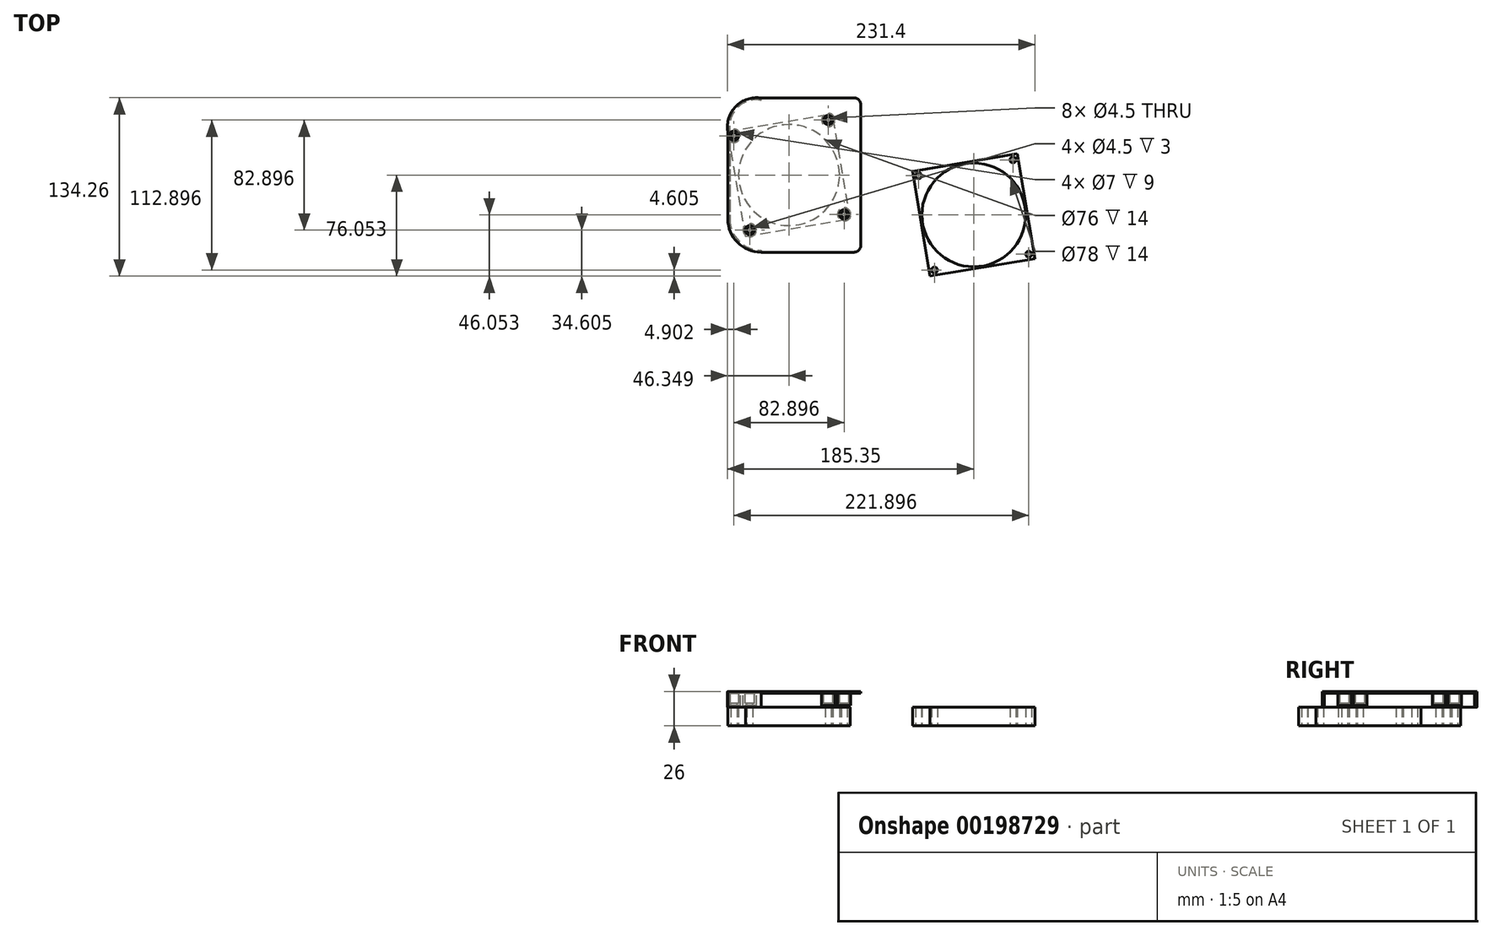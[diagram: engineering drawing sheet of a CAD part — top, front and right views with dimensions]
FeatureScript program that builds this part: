
annotation { "Feature Type Name" : "Feature", "Feature Type Description" : "" }
export const myFeature = defineFeature(function(context is Context, id is Id, definition is map)
    precondition{}
    {
        {
            var Q0;
            Q0=qCreatedBy(makeId("Top.planeOp"),FACE);
            var sketch = newSketch(context, id + "F0", { "sketchPlane" : qUnion([Q0])});
            skLineSegment(sketch, "E0.bottom", {"start": v(0, 0) * mm, "end": v(80, 0) * mm});
            skLineSegment(sketch, "E0.top", {"start": v(0, 80) * mm, "end": v(80, 80) * mm});
            skLineSegment(sketch, "E0.left", {"start": v(0, 0) * mm, "end": v(0, 80) * mm});
            skLineSegment(sketch, "E0.right", {"start": v(80, 0) * mm, "end": v(80, 80) * mm});
            skLineSegment(sketch, "E1.bottom", {"start": v(139, 50) * mm, "end": v(219, 50) * mm});
            skLineSegment(sketch, "E1.top", {"start": v(139, -30) * mm, "end": v(219, -30) * mm});
            skLineSegment(sketch, "E1.left", {"start": v(139, 50) * mm, "end": v(139, -30) * mm});
            skLineSegment(sketch, "E1.right", {"start": v(219, 50) * mm, "end": v(219, -30) * mm});
            skCircle(sketch, "E2", {"center": v(40, 40) * mm, "radius": 38 * mm});
            skCircle(sketch, "E3", {"center": v(179, 10) * mm, "radius": 39 * mm});
            skCircle(sketch, "E4", {"center": v(4, 76) * mm, "radius": 2.25 * mm});
            skCircle(sketch, "E5", {"center": v(76, 76) * mm, "radius": 2.25 * mm});
            skCircle(sketch, "E6", {"center": v(76, 4) * mm, "radius": 2.25 * mm});
            skCircle(sketch, "E7", {"center": v(4, 4) * mm, "radius": 2.25 * mm});
            skCircle(sketch, "E8", {"center": v(143, 46) * mm, "radius": 2.25 * mm});
            skCircle(sketch, "E9", {"center": v(215, 46) * mm, "radius": 2.25 * mm});
            skCircle(sketch, "E10", {"center": v(215, -26) * mm, "radius": 2.25 * mm});
            skCircle(sketch, "E11", {"center": v(143, -26) * mm, "radius": 2.25 * mm});
            skSolve(sketch);
        }
        {
            var Q0;
            Q0=qSketchRegion(id+"F0",true);
            extrude(context, id + "F1", {"entities" : qUnion([Q0]), "depth" : 14 * mm});
        }
        {
            var Q0;
            Q0=makeQuery(id+"F1.opExtrude","SWEPT_BODY",BODY,{"disambiguationData":[OSD([sQuery(id+"F0.wireOp",EDGE,"E0.bottom"),sQuery(id+"F0.wireOp",EDGE,"E0.top"),sQuery(id+"F0.wireOp",EDGE,"E0.left"),sQuery(id+"F0.wireOp",EDGE,"E0.right"),sQuery(id+"F0.wireOp",EDGE,"E2"),sQuery(id+"F0.wireOp",EDGE,"E4"),sQuery(id+"F0.wireOp",EDGE,"E5"),sQuery(id+"F0.wireOp",EDGE,"E6"),sQuery(id+"F0.wireOp",EDGE,"E7")])]});
            var Q1;
            Q1=makeQuery(id+"F1.opExtrude","SWEPT_EDGE",EDGE,{"disambiguationData":[OSD([sQuery(id+"F0.wireOp",EDGE,"E0.bottom"),sQuery(id+"F0.wireOp",EDGE,"E0.left")])]});
            transform(context, id + "F2", {"entities" : qUnion([Q0]), "transformType" : TransformType.ROTATION, "transformAxis" : qUnion([Q1]), "angle" : 9.5 * degree, "oppositeDirection" : true, "makeCopy" : false});
        }
        {
            var Q0;
            Q0=makeQuery(id+"F1.opExtrude","SWEPT_BODY",BODY,{"disambiguationData":[OSD([sQuery(id+"F0.wireOp",EDGE,"E1.bottom"),sQuery(id+"F0.wireOp",EDGE,"E1.top"),sQuery(id+"F0.wireOp",EDGE,"E1.left"),sQuery(id+"F0.wireOp",EDGE,"E1.right"),sQuery(id+"F0.wireOp",EDGE,"E3"),sQuery(id+"F0.wireOp",EDGE,"E8"),sQuery(id+"F0.wireOp",EDGE,"E9"),sQuery(id+"F0.wireOp",EDGE,"E10"),sQuery(id+"F0.wireOp",EDGE,"E11")])]});
            var Q1;
            Q1=makeQuery(id+"F1.opExtrude","SWEPT_EDGE",EDGE,{"disambiguationData":[OSD([sQuery(id+"F0.wireOp",EDGE,"E1.top"),sQuery(id+"F0.wireOp",EDGE,"E1.left")])]});
            transform(context, id + "F3", {"entities" : qUnion([Q0]), "transformType" : TransformType.ROTATION, "transformAxis" : qUnion([Q1]), "angle" : 9.5 * degree, "oppositeDirection" : true, "makeCopy" : false});
        }
        {
            var Q0;
            Q0=makeQuery(id+"F1.opExtrude","CAP_FACE",FACE,{"disambiguationData":[OSD([sQuery(id+"F0.wireOp",EDGE,"E0.bottom"),sQuery(id+"F0.wireOp",EDGE,"E0.top"),sQuery(id+"F0.wireOp",EDGE,"E0.left"),sQuery(id+"F0.wireOp",EDGE,"E0.right"),sQuery(id+"F0.wireOp",EDGE,"E2"),sQuery(id+"F0.wireOp",EDGE,"E4"),sQuery(id+"F0.wireOp",EDGE,"E5"),sQuery(id+"F0.wireOp",EDGE,"E6"),sQuery(id+"F0.wireOp",EDGE,"E7")])],"isStart":false});
            var sketch = newSketch(context, id + "F4", { "sketchPlane" : qUnion([Q0])});
            skLineSegment(sketch, "E12", {"start": v(-13.2, 78.9) * mm, "end": v(-13.2, 86.09) * mm});
            skLineSegment(sketch, "E13", {"start": v(-13.2, 78.9) * mm, "end": v(-13.2, 13) * mm});
            skLineSegment(sketch, "E14", {"start": v(11.8, -12) * mm, "end": v(86.8, -12) * mm});
            skLineSegment(sketch, "E15", {"start": v(86.8, -12) * mm, "end": v(86.8, 104.16) * mm});
            skLineSegment(sketch, "E16", {"start": v(4.61, 103.95) * mm, "end": v(86.8, 104.16) * mm});
            skArc(sketch, "E17", {"start": v(11.8, 103.97) * mm, "mid": v(-7.15, 97.86) * mm, "end": v(-13.2, 78.9) * mm});
            skArc(sketch, "E18", {"start": v(-13.2, 13) * mm, "mid": v(-5.88, -4.68) * mm, "end": v(11.8, -12) * mm});
            skPoint(sketch, "E19.orphan", {"position": v(-13.2, 103.9) * mm});
            skPoint(sketch, "E20.orphan", {"position": v(-13.2, -12) * mm});
            skSolve(sketch);
        }
        {
            var Q0;
            Q0 = qSketchRegion(id + "F4", true);
            extrude(context, id + "F5", {"entities" : qUnion([Q0]), "depth" : 12 * mm});
        }
        {
            var Q0;
            Q0=makeQuery(id+"F5.opExtrude","CAP_FACE",FACE,{"disambiguationData":[OSD([sQuery(id+"F4.wireOp",EDGE,"E13"),sQuery(id+"F4.wireOp",EDGE,"E14"),sQuery(id+"F4.wireOp",EDGE,"E15"),sQuery(id+"F4.wireOp",EDGE,"E16"),sQuery(id+"F4.wireOp",EDGE,"E17"),sQuery(id+"F4.wireOp",EDGE,"E18")])],"isStart":false});
            var sketch = newSketch(context, id + "F6", { "sketchPlane" : qUnion([Q0])});
            skCircle(sketch, "E21", {"center": v(3.28, 4.6) * mm, "radius": 2.25 * mm});
            skCircle(sketch, "E22", {"center": v(74.3, 16.49) * mm, "radius": 2.25 * mm});
            skCircle(sketch, "E23", {"center": v(-8.6, 75.62) * mm, "radius": 2.25 * mm});
            skCircle(sketch, "E24", {"center": v(62.41, 87.5) * mm, "radius": 2.25 * mm});
            skSolve(sketch);
        }
        {
            var Q0;
            Q0 = qSketchRegion(id + "F6", true);
            extrude(context, id + "F7", {"entities" : qUnion([Q0]), "operationType" : NewBodyOperationType.REMOVE, "endBound" : BoundingType.UP_TO_NEXT, "oppositeDirection" : true, "depth" : 25 * mm});
        }
        {
            var Q0;
            Q0=makeQuery(id+"F5.opExtrude","CAP_FACE",FACE,{"disambiguationData":[OSD([sQuery(id+"F4.wireOp",EDGE,"E13"),sQuery(id+"F4.wireOp",EDGE,"E14"),sQuery(id+"F4.wireOp",EDGE,"E15"),sQuery(id+"F4.wireOp",EDGE,"E16"),sQuery(id+"F4.wireOp",EDGE,"E17"),sQuery(id+"F4.wireOp",EDGE,"E18")])],"isStart":false});
            var sketch = newSketch(context, id + "F8", { "sketchPlane" : qUnion([Q0])});
            skCircle(sketch, "E25", {"center": v(62.41, 87.5) * mm, "radius": 3.5 * mm});
            skCircle(sketch, "E26", {"center": v(-8.6, 75.62) * mm, "radius": 3.5 * mm});
            skCircle(sketch, "E27", {"center": v(3.28, 4.6) * mm, "radius": 3.5 * mm});
            skCircle(sketch, "E28", {"center": v(74.3, 16.49) * mm, "radius": 3.5 * mm});
            skSolve(sketch);
        }
        {
            var Q0;
            Q0 = qSketchRegion(id + "F8", true);
            extrude(context, id + "F9", {"entities" : qUnion([Q0]), "operationType" : NewBodyOperationType.REMOVE, "oppositeDirection" : true, "depth" : 9 * mm});
        }
        {
            var Q0;
            Q0=makeQuery(id+"F5.opExtrude","SWEPT_FACE",FACE,{"disambiguationData":[OSD([sQuery(id+"F4.wireOp",EDGE,"E15")])]});
            var Q1;
            Q1=makeQuery(id+"F5.opExtrude","SWEPT_FACE",FACE,{"disambiguationData":[OSD([sQuery(id+"F4.wireOp",EDGE,"E14")])]});
            var Q2;
            Q2=makeQuery(id+"F5.opExtrude","CAP_FACE",FACE,{"disambiguationData":[OSD([sQuery(id+"F4.wireOp",EDGE,"E13"),sQuery(id+"F4.wireOp",EDGE,"E14"),sQuery(id+"F4.wireOp",EDGE,"E15"),sQuery(id+"F4.wireOp",EDGE,"E16"),sQuery(id+"F4.wireOp",EDGE,"E17"),sQuery(id+"F4.wireOp",EDGE,"E18")])],"isStart":true});
            shell(context, id + "F10", {"entities" : qUnion([Q0, Q1, Q2]), "thickness" : 1.5 * mm});
        }
        {
            var Q0;
            Q0=makeQuery(id+"F5.opExtrude","SWEPT_FACE",FACE,{"disambiguationData":[OSD([sQuery(id+"F4.wireOp",EDGE,"E16")])]});
            var sketch = newSketch(context, id + "F11", { "sketchPlane" : qUnion([Q0])});
            skLineSegment(sketch, "E29.bottom", {"start": v(-87.07, 14) * mm, "end": v(-12.06, 14) * mm});
            skLineSegment(sketch, "E29.top", {"start": v(-87.07, 24.5) * mm, "end": v(-12.06, 24.5) * mm});
            skLineSegment(sketch, "E29.left", {"start": v(-87.07, 14) * mm, "end": v(-87.07, 24.5) * mm});
            skLineSegment(sketch, "E29.right", {"start": v(-12.06, 14) * mm, "end": v(-12.06, 24.5) * mm});
            skSolve(sketch);
        }
        {
            var Q0;
            Q0 = qSketchRegion(id + "F11", true);
            extrude(context, id + "F12", {"entities" : qUnion([Q0]), "operationType" : NewBodyOperationType.REMOVE, "endBound" : BoundingType.UP_TO_NEXT, "oppositeDirection" : true, "depth" : 1.5 * mm});
        }
        {
            var Q0;
            Q0=makeQuery(id+"F5.opExtrude","SWEPT_EDGE",EDGE,{"disambiguationData":[OSD([sQuery(id+"F4.wireOp",EDGE,"E14"),sQuery(id+"F4.wireOp",EDGE,"E15")])]});
            var Q1;
            Q1=makeQuery(id+"F5.opExtrude","SWEPT_EDGE",EDGE,{"disambiguationData":[OSD([sQuery(id+"F4.wireOp",EDGE,"E15"),sQuery(id+"F4.wireOp",EDGE,"E16")])]});
            fillet(context, id + "F13", {"entities" : qUnion([Q0, Q1]), "radius" : 5 * mm, "tangentPropagation" : true, "allowEdgeOverflow" : false});
        }
    });
